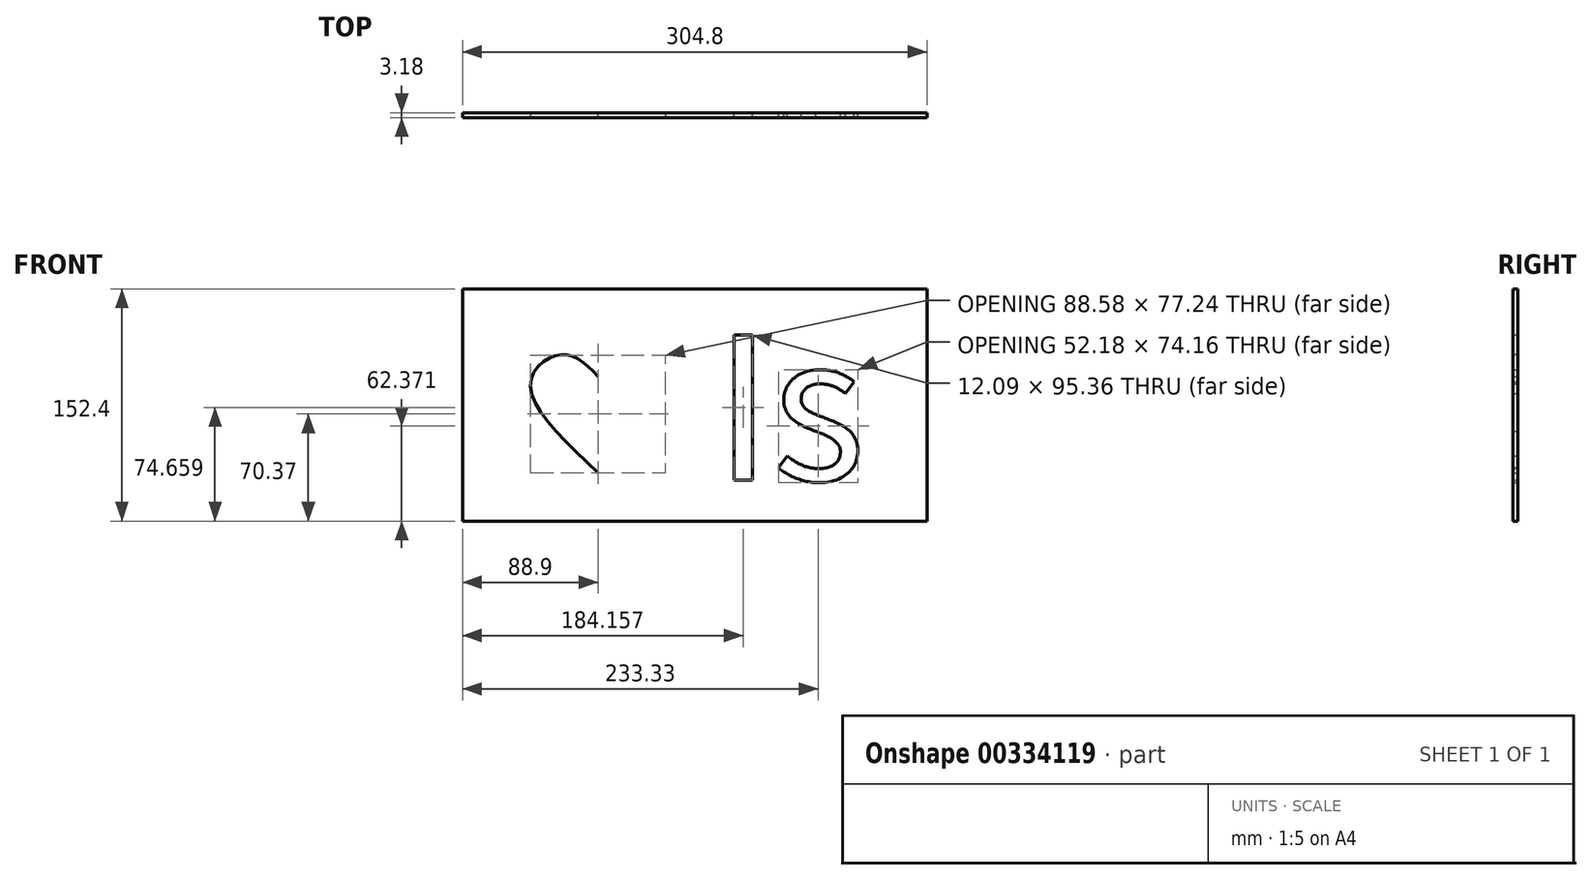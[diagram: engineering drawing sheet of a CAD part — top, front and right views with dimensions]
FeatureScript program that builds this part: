
annotation { "Feature Type Name" : "Feature", "Feature Type Description" : "" }
export const myFeature = defineFeature(function(context is Context, id is Id, definition is map)
    precondition{}
    {
        {
            var Q0;
            Q0=qCreatedBy(makeId("Front.planeOp"),FACE);
            var sketch = newSketch(context, id + "F0", { "sketchPlane" : qUnion([Q0])});
            skLineSegment(sketch, "E0.bottom", {"start": v(-152.4, 76.2) * mm, "end": v(152.4, 76.2) * mm});
            skLineSegment(sketch, "E0.top", {"start": v(-152.4, -76.2) * mm, "end": v(152.4, -76.2) * mm});
            skLineSegment(sketch, "E0.left", {"start": v(-152.4, 76.2) * mm, "end": v(-152.4, -76.2) * mm});
            skLineSegment(sketch, "E0.right", {"start": v(152.4, 76.2) * mm, "end": v(152.4, -76.2) * mm});
            skPoint(sketch, "E0.middle", {"position": v(0, 0) * mm});
            skText(sketch, "E1", { "text": "Is", "fontName": "NotoSansCJKtc-Regular.otf"});
            skLineSegment(sketch, "E2.bottom", {"start": v(-107.95, 44.45) * mm, "end": v(-19.05, 44.45) * mm, "construction": true});
            skLineSegment(sketch, "E2.top", {"start": v(-107.95, -44.45) * mm, "end": v(-19.05, -44.45) * mm, "construction": true});
            skLineSegment(sketch, "E2.left", {"start": v(-107.95, 44.45) * mm, "end": v(-107.95, -44.45) * mm, "construction": true});
            skLineSegment(sketch, "E2.right", {"start": v(-19.05, 44.45) * mm, "end": v(-19.05, -44.45) * mm, "construction": true});
            skPoint(sketch, "E2.middle", {"position": v(-63.5, 0) * mm});
            skLineSegment(sketch, "E3", {"start": v(-63.5, 44.45) * mm, "end": v(-63.5, -44.45) * mm, "construction": true});
            skFitSpline(sketch, "E4", {"points": [v(-63.5, 18.8) * mm, v(-47.43, 31.75) * mm, v(-31.43, 30.8) * mm, v(-19.05, 12.22) * mm, v(-63.5, -44.45) * mm], "startDerivative": vector(74.19, 76.17) * mm, "endDerivative": vector(-168.7, -159.22) * mm});
            skFitSpline(sketch, "E5.MirrorCS", {"points": [v(-63.5, 18.8) * mm, v(-79.57, 31.75) * mm, v(-95.57, 30.8) * mm, v(-107.95, 12.22) * mm, v(-63.5, -44.45) * mm], "startDerivative": vector(-74.19, 76.17) * mm, "endDerivative": vector(168.7, -159.22) * mm});
            const initialGuessF0  = {"E1": [0.0127, -0.04922, 1, 0, 0.09367]};
            skSetInitialGuess(sketch, initialGuessF0);
            skSolve(sketch);
        }
        {
            var Q0;
            Q0=qSketchRegion(id+"F0",true);
            extrude(context, id + "F1", {"entities" : qUnion([Q0]), "depth" : 3.17 * mm});
        }
    });
